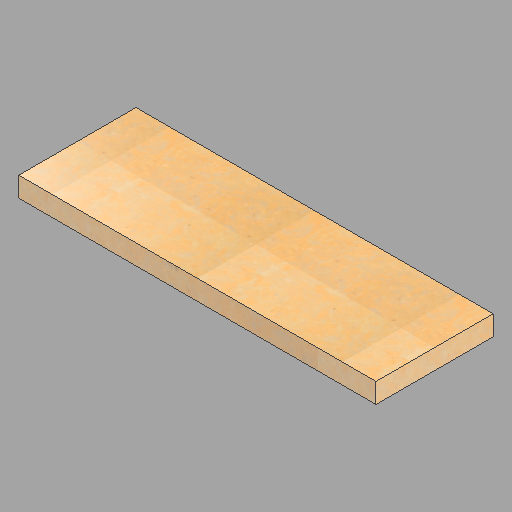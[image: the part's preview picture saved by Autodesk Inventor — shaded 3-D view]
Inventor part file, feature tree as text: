
AUTODESK INVENTOR PART (.ipt)
format: ipt  version: 2023 (Build 270158030, 158C)  size: 220,160 bytes
history: native  units: in
note: dims shown in document units (in); Inventor stores cm internally (conversion verified against a paired STEP export)
features: extrude x1, sketch x1
ambient origin geometry x8: Origin, YZ Plane, XZ Plane, XY Plane, X Axis, Y Axis, Z Axis, Center Point
bodies: Solid1 (feature_tree)
feature tree (2):
  extrude  "Extrusion1"  Depth=23.5in
  sketch  "Sketch1"  dims[d0=71.625in d1=23.5in d2=4.0in d3=0.0in]
